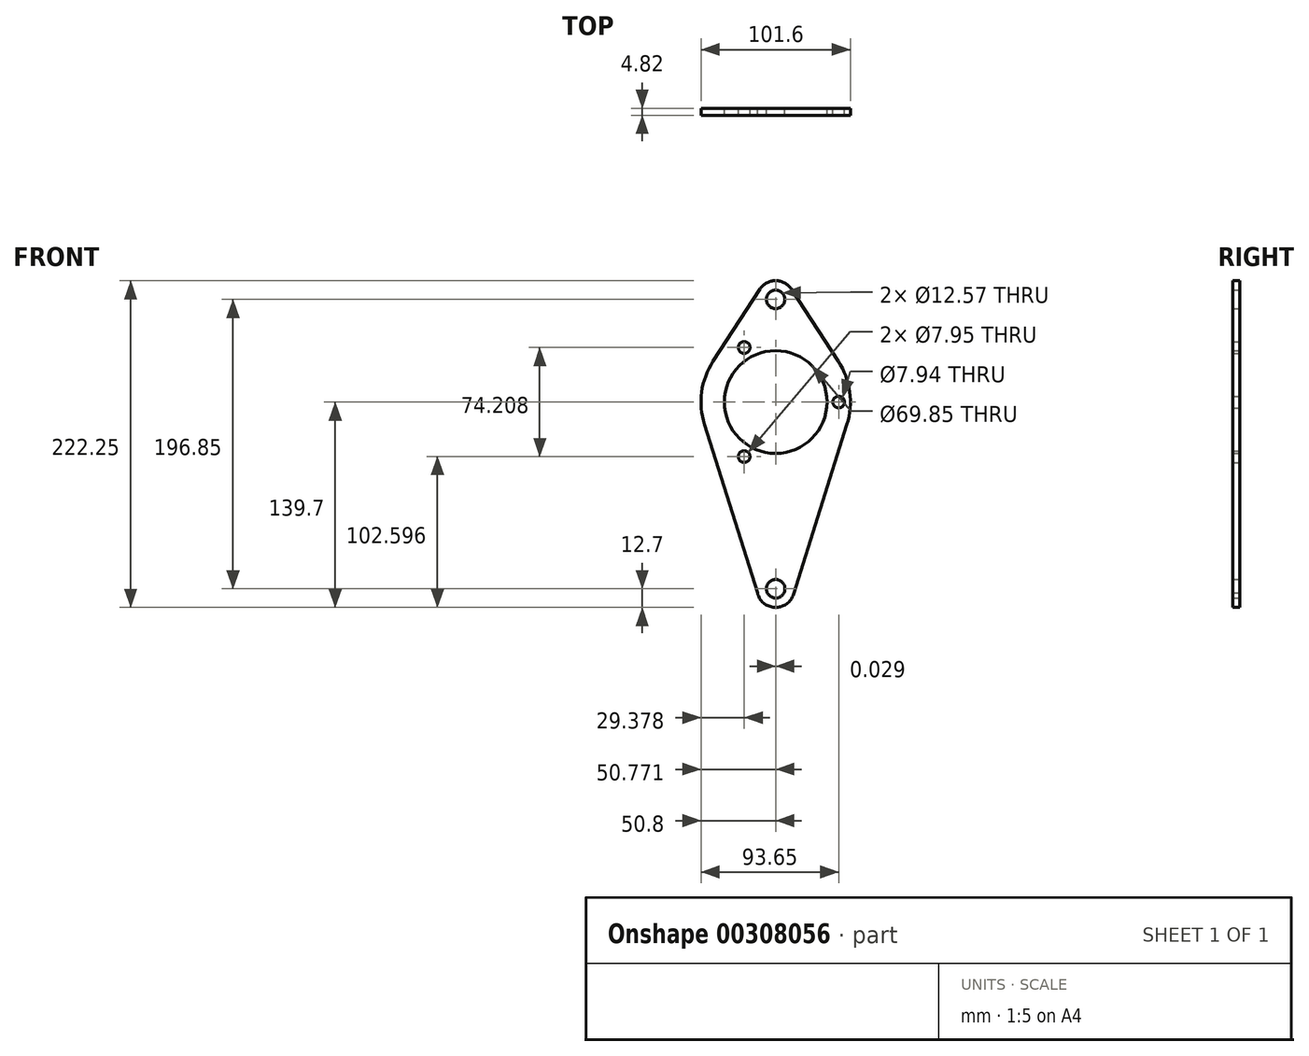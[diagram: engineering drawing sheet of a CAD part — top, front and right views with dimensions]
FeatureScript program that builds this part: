
annotation { "Feature Type Name" : "Feature", "Feature Type Description" : "" }
export const myFeature = defineFeature(function(context is Context, id is Id, definition is map)
    precondition{}
    {
        {
            var Q0;
            Q0=qCreatedBy(makeId("Front.planeOp"),FACE);
            var sketch = newSketch(context, id + "F0", { "sketchPlane" : qUnion([Q0])});
            skArc(sketch, "E0", {"start": v(10.61, 76.78) * mm, "mid": v(-0.03, 82.55) * mm, "end": v(-10.68, 76.77) * mm});
            skArc(sketch, "E1", {"start": v(-12.4, -129.73) * mm, "mid": v(-0.56, -139.69) * mm, "end": v(12.12, -130.8) * mm});
            skLineSegment(sketch, "E2", {"start": v(-12.4, -129.73) * mm, "end": v(-48.45, -15.26) * mm});
            skLineSegment(sketch, "E3", {"start": v(12.12, -130.8) * mm, "end": v(48.46, -15.24) * mm});
            skLineSegment(sketch, "E4", {"start": v(-42.59, 27.7) * mm, "end": v(-10.68, 76.77) * mm});
            skLineSegment(sketch, "E5", {"start": v(42.57, 27.73) * mm, "end": v(10.61, 76.78) * mm});
            skCircle(sketch, "E6", {"center": v(-0.03, 69.85) * mm, "radius": 6.29 * mm});
            skCircle(sketch, "E7", {"center": v(0, -127) * mm, "radius": 6.29 * mm});
            skCircle(sketch, "E8", {"center": v(42.85, 0) * mm, "radius": 3.97 * mm});
            skCircle(sketch, "E9", {"center": v(-21.42, 37.1) * mm, "radius": 3.98 * mm});
            skCircle(sketch, "E10.MirrorC", {"center": v(-21.42, -37.1) * mm, "radius": 3.98 * mm});
            skArc(sketch, "E11", {"start": v(48.46, -15.24) * mm, "mid": v(50.33, 6.9) * mm, "end": v(42.57, 27.73) * mm});
            skArc(sketch, "E12.trimOffspring", {"start": v(-42.59, 27.7) * mm, "mid": v(-50.33, 6.87) * mm, "end": v(-48.45, -15.26) * mm});
            skCircle(sketch, "E13", {"center": v(0, 0) * mm, "radius": 34.93 * mm});
            skLineSegment(sketch, "E14", {"start": v(0, 0) * mm, "end": v(-21.42, 37.1) * mm});
            skLineSegment(sketch, "E15", {"start": v(0, 0) * mm, "end": v(-21.42, -37.1) * mm});
            skSolve(sketch);
        }
        {
            var Q0;
            Q0=qSketchRegion(id+"F0",true);
            extrude(context, id + "F1", {"entities" : qUnion([Q0]), "endBound" : BoundingType.SYMMETRIC, "depth" : 4.83 * mm, "offsetDistance" : 25.4 * mm});
        }
    });
